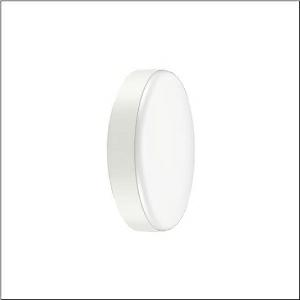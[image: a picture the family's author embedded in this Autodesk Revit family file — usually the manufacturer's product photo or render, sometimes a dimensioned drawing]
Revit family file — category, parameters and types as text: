
# Revit family: rondel_31_51wc10db34a
name_source: partatom
category: Lighting Fixtures
units: mm (PartAtom-declared; Revit-internal decimal feet)

## family parameters
Cut with Voids When Loaded = No
Host = Face
Light Source = No
Part Type = Normal
Room Calculation Point = No
Round Connector Dimension = Use Diameter
Shared = No

## types (1)
- Rondel 31 (1 x LED, 4250 lm, 34 W, 3000K)
    Apparent Load = 34 VA
    CIE Flux Codes = 44 75 94 94 100
    Color Rendering = 80
    Color Temperature = 3000K
    Default Elevation = 1800 mm
    Description = Rondel 31, wall and ceiling luminaire, primary optical cover: cover, of PC, opal, light emission: direct distribution, primary light characteristic: symmetric, installation type: surface-mounted, LED, rated luminous flux: 4.100lm, luminous efficacy: 120lm/W, light colour: 830, colour temperature: 3000K, with terminal, 5-pole, max. 2.5mm², mains connection: 220..240V, AC, 50/60Hz, rated input power: 34W, luminaire housing, of PC, traffic white (RAL 9016), diameter: 480mm, protection rating (complete): IP65, insulation class (complete): insulation class II (safety insulation), certification: CE, impact resistance: IK10, permissible storage temperature: -20..+60°C, packaging unit: 1 piece
    Height = 97 mm
    Lamp = 1 x LED
    Lamp Light Flux = 4250 lm
    Lamp Power = 34 W
    Lamp count = 1
    Length = 480 mm
    Luminous efficacy = 125 lm/W
    Manufacturer = Siteco
    ModVariant = No
    Model = 51WC10DB34A
    Mounting Place = Ceiling
    Mounting Type = Surface mounted
    Number of Poles = 1
    OnlyDefault = Yes
    Power Factor = 1
    Product Name = Rondel 31
    Product group = wall and ceiling luminaire
    ProductGroupID = 301
    Protection Class = Protection class II
    Protection Degree = IP 65
    RLX_Detail_Level = 1
    RlxData = <blob elided: 40725 chars, md5=ab72c18d>
    Socket = socket
    Standby Power = 0 W
    System Light Flux = 4250 lm
    System Power = 34 W
    Type Comments = Product without accessories
    Type Image = l_1007188.jpg
    URL = http://relux.com
    VarID = ---
    Voltage = 0 V
    Weight = 0.00 kg
    Width = 0 mm  [stored 0 ft]

note: [stored X ft] marks values corroborated as IEEE doubles in the binary element streams (Revit-internal decimal feet)

## geometry (parser evidence)
native form markers: Blend x4, Sweep x14
no freeform markers — native parametric forms only
